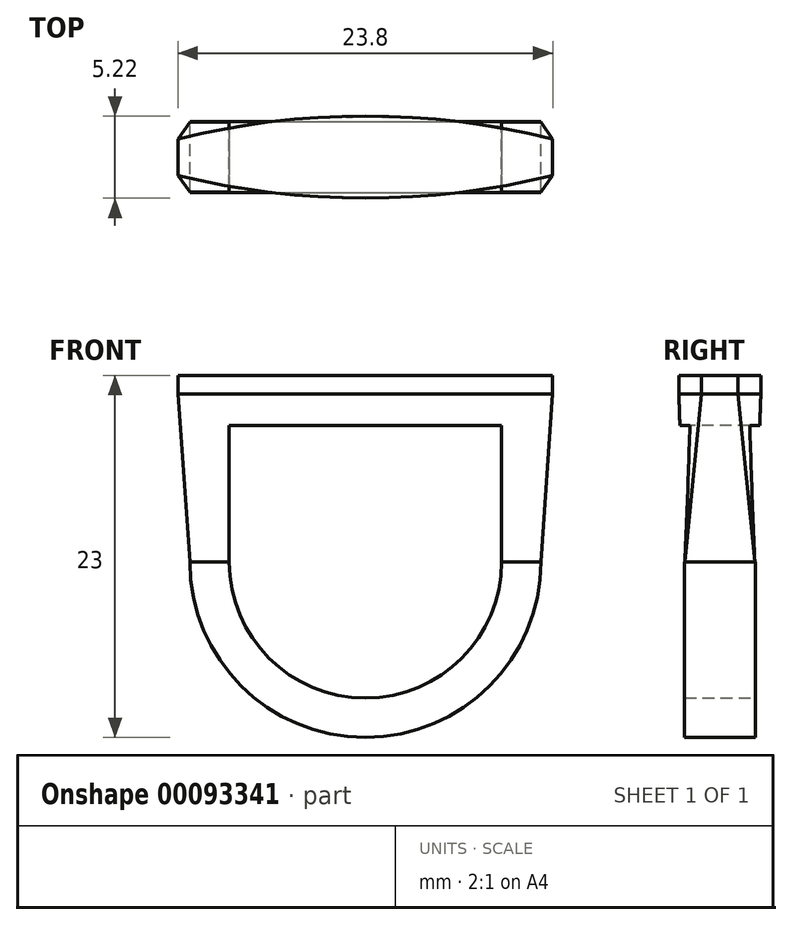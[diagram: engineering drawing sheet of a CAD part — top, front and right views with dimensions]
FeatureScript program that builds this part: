
annotation { "Feature Type Name" : "Feature", "Feature Type Description" : "" }
export const myFeature = defineFeature(function(context is Context, id is Id, definition is map)
    precondition{}
    {
        {
            var Q0;
            Q0=qCreatedBy(makeId("Front.planeOp"),FACE);
            var sketch = newSketch(context, id + "F0", { "sketchPlane" : qUnion([Q0])});
            skCircle(sketch, "E0", {"center": v(0, 0) * mm, "radius": 8.65 * mm});
            skCircle(sketch, "E1.0", {"center": v(0, 0) * mm, "radius": 11.15 * mm});
            skPoint(sketch, "E2", {"position": v(11.15, 0) * mm});
            skPoint(sketch, "E3", {"position": v(-11.15, 0) * mm});
            skLineSegment(sketch, "E4", {"start": v(11.15, 0) * mm, "end": v(11.15, 11.15) * mm});
            skLineSegment(sketch, "E5", {"start": v(11.15, 11.15) * mm, "end": v(0, 11.15) * mm});
            skLineSegment(sketch, "E6.MirrorCS", {"start": v(-11.15, 11.15) * mm, "end": v(0, 11.15) * mm});
            skLineSegment(sketch, "E7.MirrorCS", {"start": v(-11.15, 0) * mm, "end": v(-11.15, 11.15) * mm});
            skLineSegment(sketch, "E8", {"start": v(0, 8.65) * mm, "end": v(11.15, 8.65) * mm});
            skLineSegment(sketch, "E9", {"start": v(0, 8.65) * mm, "end": v(0, 9.75) * mm, "construction": true});
            skLineSegment(sketch, "E10", {"start": v(0, 9.75) * mm, "end": v(11.15, 9.75) * mm});
            skLineSegment(sketch, "E11.MirrorCS", {"start": v(0, 9.75) * mm, "end": v(-11.15, 9.75) * mm});
            skLineSegment(sketch, "E12.MirrorCS", {"start": v(0, 8.65) * mm, "end": v(-11.15, 8.65) * mm});
            skPoint(sketch, "E13", {"position": v(-8.65, 0) * mm});
            skPoint(sketch, "E14", {"position": v(8.65, 0) * mm});
            skLineSegment(sketch, "E15", {"start": v(-8.65, 0) * mm, "end": v(-8.65, 8.65) * mm});
            skLineSegment(sketch, "E16", {"start": v(8.65, 0) * mm, "end": v(8.65, 8.65) * mm});
            skLineSegment(sketch, "E17", {"start": v(11.15, 0) * mm, "end": v(8.65, 0) * mm});
            skLineSegment(sketch, "E18", {"start": v(-11.15, 0) * mm, "end": v(-8.65, 0) * mm});
            skLineSegment(sketch, "E19", {"start": v(-8.65, 0) * mm, "end": v(8.65, 0) * mm});
            skSolve(sketch);
        }
        {
            var Q0;
            {var subQ2=sQuery(id+"F0.wireOp",EDGE,"E17");Q0=makeQuery(id+"F0.imprint","IMPRINT",FACE,{"disambiguationData":[TD([[makeQuery(id+"F0.imprint","IMPRINT",EDGE,{"derivedFrom":subQ2}),1.0]])]});}
            extrude(context, id + "F1", {"entities" : qUnion([Q0]), "depth" : 2.25 * mm, "hasSecondDirection" : true, "secondDirectionOppositeDirection" : true, "secondDirectionDepth" : 2.25 * mm});
        }
        {
            var Q0;
            Q0=qCreatedBy(makeId("Top.planeOp"),FACE);
            var sketch = newSketch(context, id + "F2", { "sketchPlane" : qUnion([Q0])});
            skLineSegment(sketch, "E20", {"start": v(-11.9, 0) * mm, "end": v(-11.9, -1.16) * mm});
            skLineSegment(sketch, "E21.MirrorCS", {"start": v(11.9, 0) * mm, "end": v(11.9, -1.16) * mm});
            skLineSegment(sketch, "E22.MirrorCS", {"start": v(11.9, 0) * mm, "end": v(11.9, 1.16) * mm});
            skLineSegment(sketch, "E23.MirrorCS", {"start": v(-11.9, 0) * mm, "end": v(-11.9, 1.16) * mm});
            skArc(sketch, "E24", {"start": v(-11.9, -1.16) * mm, "mid": v(0, -2.6) * mm, "end": v(11.9, -1.16) * mm});
            skArc(sketch, "E25.MirrorCS", {"start": v(-11.9, 1.16) * mm, "mid": v(0, 2.6) * mm, "end": v(11.9, 1.16) * mm});
            skSolve(sketch);
        }
        {
            var Q0;
            Q0=makeQuery(id+"F2.imprint","IMPRINT",FACE,{"disambiguationData":[TD([[makeQuery(id+"F2.imprint","IMPRINT",EDGE,{"derivedFrom":sQuery(id+"F2.wireOp",EDGE,"E20")}),1.0]])]});
            extrude(context, id + "F3", {"entities" : qUnion([Q0]), "depth" : 11.85 * mm, "hasSecondDirection" : true, "secondDirectionOppositeDirection" : false, "secondDirectionDepth" : 10.65 * mm});
        }
        {
            var Q0;
            Q0=qCreatedBy(makeId("Top.planeOp"),FACE);
            var sketch = newSketch(context, id + "F4", { "sketchPlane" : qUnion([Q0])});
            skLineSegment(sketch, "E26.bottom", {"start": v(-11.13, -2.23) * mm, "end": v(11.13, -2.23) * mm});
            skLineSegment(sketch, "E26.top", {"start": v(-11.13, 2.23) * mm, "end": v(11.13, 2.23) * mm});
            skLineSegment(sketch, "E26.left", {"start": v(-11.13, -2.23) * mm, "end": v(-11.13, 2.23) * mm});
            skLineSegment(sketch, "E26.right", {"start": v(11.13, -2.23) * mm, "end": v(11.13, 2.23) * mm});
            skPoint(sketch, "E26.middle", {"position": v(0, 0) * mm});
            skSolve(sketch);
        }
        {
            var Q0;
            Q0=makeQuery(id+"F4.imprint","IMPRINT",FACE,{"disambiguationData":[TD([[makeQuery(id+"F4.imprint","IMPRINT",EDGE,{"derivedFrom":sQuery(id+"F4.wireOp",EDGE,"E26.bottom")}),1.0]])]});
            var Q1;
            Q1=makeQuery(id+"F3.opExtrude","CAP_FACE",FACE,{"disambiguationData":[OSD([sQuery(id+"F2.wireOp",EDGE,"E20"),sQuery(id+"F2.wireOp",EDGE,"E21.MirrorCS"),sQuery(id+"F2.wireOp",EDGE,"E22.MirrorCS"),sQuery(id+"F2.wireOp",EDGE,"E23.MirrorCS"),sQuery(id+"F2.wireOp",EDGE,"E24"),sQuery(id+"F2.wireOp",EDGE,"E25.MirrorCS")])],"isStart":true});
            loft(context, id + "F5", {"sheetProfilesArray" : [{ "sheetProfileEntities" : qUnion([Q0]) }, { "sheetProfileEntities" : qUnion([Q1]) }]});
        }
        {
            var Q0;
            {var subQ2=sQuery(id+"F0.wireOp",EDGE,"E19");Q0=makeQuery(id+"F0.imprint","IMPRINT",FACE,{"disambiguationData":[TD([[makeQuery(id+"F0.imprint","IMPRINT",EDGE,{"derivedFrom":subQ2}),1.0]])]});}
            var Q1;
            {var subQ3=sQuery(id+"F0.wireOp",EDGE,"E16");var subQ5=sQuery(id+"F0.wireOp",EDGE,"E1.0");var subQ6=makeQuery(id+"F0.imprint","INTERSECT",VERTEX,{"derivedFrom":[subQ5,subQ3]});Q1=makeQuery(id+"F0.imprint","IMPRINT",FACE,{"disambiguationData":[TD([[makeQuery(id+"F0.imprint","IMPRINT",EDGE,{"disambiguationData":[TD([[subQ6,-1.0]])],"derivedFrom":subQ5}),1.0]])]});}
            var Q2;
            {var subQ0=sQuery(id+"F0.wireOp",EDGE,"E16");var subQ1=sQuery(id+"F0.wireOp",EDGE,"E1.0");var subQ2=makeQuery(id+"F0.imprint","INTERSECT",VERTEX,{"derivedFrom":[subQ1,subQ0]});Q2=makeQuery(id+"F0.imprint","IMPRINT",FACE,{"disambiguationData":[TD([[makeQuery(id+"F0.imprint","IMPRINT",EDGE,{"disambiguationData":[TD([[subQ2,-1.0]])],"derivedFrom":subQ1}),-1.0]])]});}
            var Q3;
            {var subQ0=sQuery(id+"F0.wireOp",EDGE,"E12.MirrorCS");var subQ5=sQuery(id+"F0.wireOp",EDGE,"E1.0");var subQ6=makeQuery(id+"F0.imprint","INTERSECT",VERTEX,{"derivedFrom":[subQ5,subQ0]});Q3=makeQuery(id+"F0.imprint","IMPRINT",FACE,{"disambiguationData":[TD([[makeQuery(id+"F0.imprint","IMPRINT",EDGE,{"disambiguationData":[TD([[subQ6,-1.0]])],"derivedFrom":subQ5}),1.0]])]});}
            var Q4;
            {var subQ0=sQuery(id+"F0.wireOp",EDGE,"E12.MirrorCS");var subQ1=sQuery(id+"F0.wireOp",EDGE,"E1.0");var subQ2=makeQuery(id+"F0.imprint","INTERSECT",VERTEX,{"derivedFrom":[subQ1,subQ0]});Q4=makeQuery(id+"F0.imprint","IMPRINT",FACE,{"disambiguationData":[TD([[makeQuery(id+"F0.imprint","IMPRINT",EDGE,{"disambiguationData":[TD([[subQ2,-1.0]])],"derivedFrom":subQ1}),-1.0]])]});}
            extrude(context, id + "F6", {"entities" : qUnion([Q0, Q1, Q2, Q3, Q4]), "operationType" : NewBodyOperationType.REMOVE, "oppositeDirection" : true, "depth" : 25 * mm, "hasSecondDirection" : true, "secondDirectionOppositeDirection" : false, "secondDirectionDepth" : 25 * mm});
        }
    });
